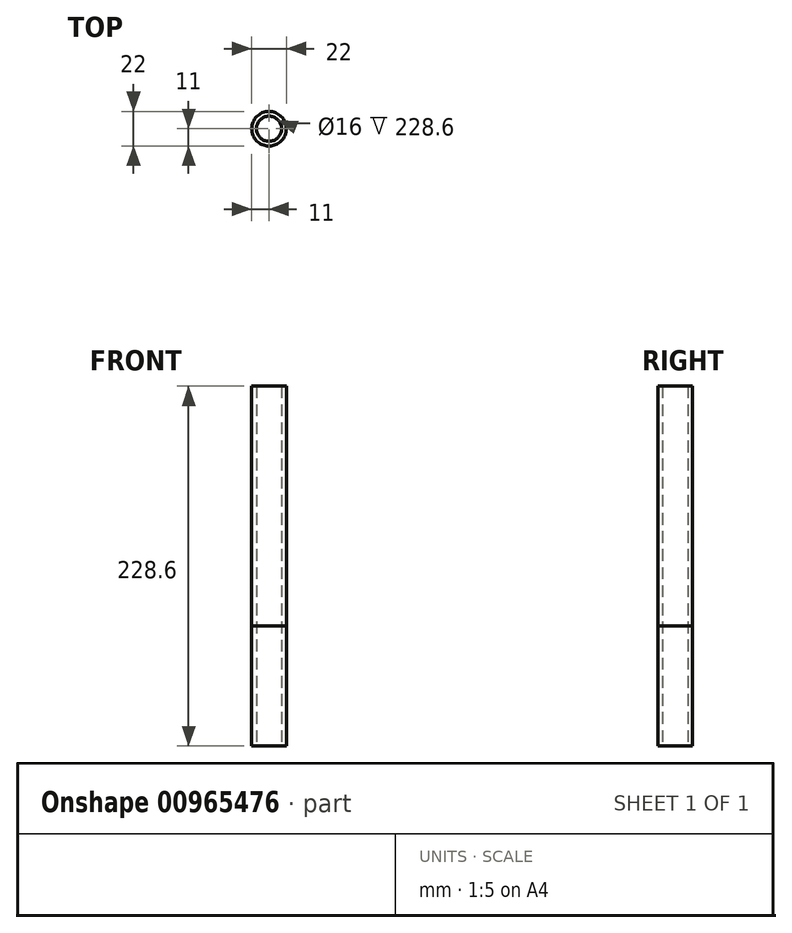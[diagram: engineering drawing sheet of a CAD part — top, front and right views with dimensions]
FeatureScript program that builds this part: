
annotation { "Feature Type Name" : "Feature", "Feature Type Description" : "" }
export const myFeature = defineFeature(function(context is Context, id is Id, definition is map)
    precondition{}
    {
        {
            var Q0;
            Q0=qCreatedBy(makeId("Top.planeOp"),FACE);
            var sketch = newSketch(context, id + "F0", { "sketchPlane" : qUnion([Q0])});
            skCircle(sketch, "E0", {"center": v(0, 0) * mm, "radius": 8 * mm});
            skCircle(sketch, "E1", {"center": v(0, 0) * mm, "radius": 11 * mm});
            skSolve(sketch);
        }
        {
            var Q0;
            Q0=makeQuery(id+"F0.imprint","IMPRINT",FACE,{"disambiguationData":[TD([[makeQuery(id+"F0.imprint","IMPRINT",EDGE,{"derivedFrom":sQuery(id+"F0.wireOp",EDGE,"E0")}),-1.0]])]});
            extrude(context, id + "F1", {"entities" : qUnion([Q0]), "depth" : 228.6 * mm, "offsetDistance" : 25.4 * mm});
        }
        {
            var Q0;
            Q0=qCreatedBy(makeId("Top.planeOp"),FACE);
            cPlane(context, id + "F2", {"entities" : qUnion([Q0]), "cplaneType" : CPlaneType.OFFSET, "offset" : 76.2 * mm, "width" : 152.4 * mm, "height" : 152.4 * mm});
        }
        {
            var Q0;
            Q0=qCreatedBy(id+"F2.planeOp",FACE);
            var sketch = newSketch(context, id + "F3", { "sketchPlane" : qUnion([Q0])});
            skCircle(sketch, "E2", {"center": v(0, 0) * mm, "radius": 18.86 * mm});
            skCircle(sketch, "E3", {"center": v(0, 0) * mm, "radius": 10.99 * mm});
            skSolve(sketch);
        }
        {
            var Q0;
            Q0=makeQuery(id+"F3.imprint","IMPRINT",FACE,{"disambiguationData":[TD([[makeQuery(id+"F3.imprint","IMPRINT",EDGE,{"derivedFrom":sQuery(id+"F3.wireOp",EDGE,"E2")}),1.0]])]});
            extrude(context, id + "F4", {"entities" : qUnion([Q0]), "operationType" : NewBodyOperationType.REMOVE, "depth" : .1 * mm, "offsetDistance" : 25.4 * mm});
        }
    });
